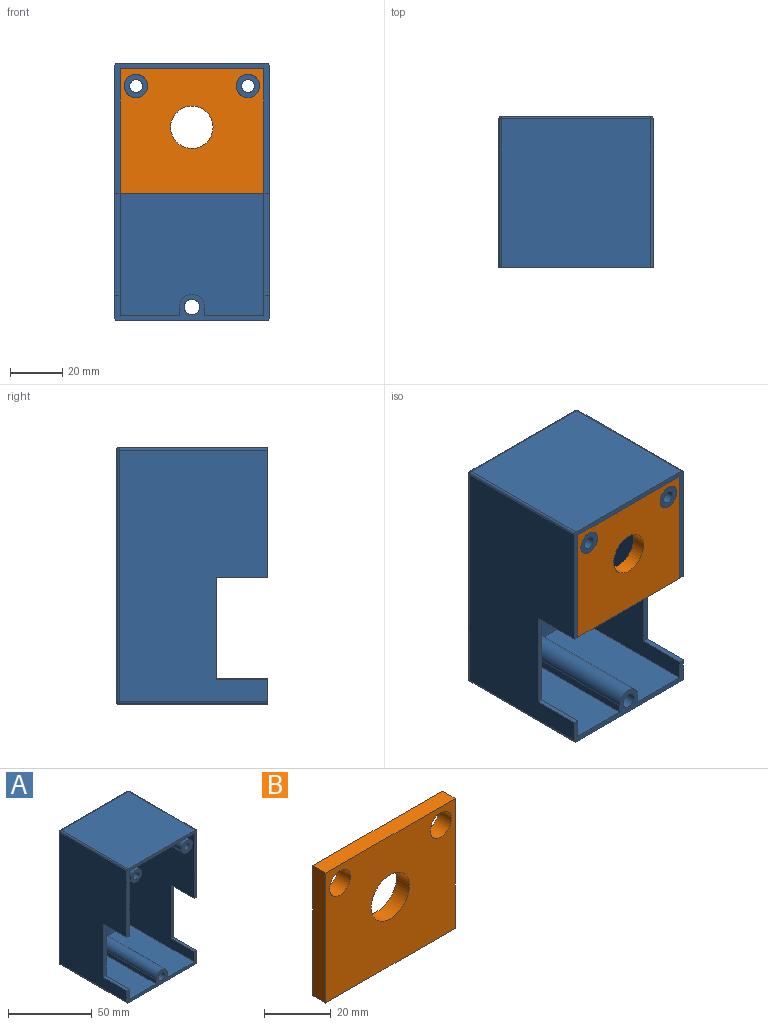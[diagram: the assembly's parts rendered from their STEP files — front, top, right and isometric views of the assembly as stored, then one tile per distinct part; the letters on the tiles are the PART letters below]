
ASSEMBLY  parts=2 mates=1
PART A: 53 faces, bbox 58.9x57.6x98 mm
  f0: cylinder r=15.9mm len=31.11mm, axis (0,1,0), area 179.6mm2, adj f3,f4,f47,f51
  f1: cylinder r=15.9mm len=31.11mm, axis (0,1,0), area 179.6mm2, adj f3,f5,f48,f50
  f2: cylinder r=17.91mm len=35.19mm, axis (0,1,0), area 106.6mm2, adj f4,f7,f47,f51
  f3: plane 96x56.9mm, normal (0,1,0), area 4575.9mm2, adj f0,f1,f15,f17,f34,f38,f39,f43
  f4: plane 35.19x14.59mm, normal (0,-1,0), area 92.9mm2, adj f0,f2,f47,f51
  f5: plane 35.19x14.59mm, normal (0,-1,0), area 92.9mm2, adj f1,f10,f48,f50
  f6: plane 55.55x22.69mm, normal (0,0,1), area 1260.4mm2, adj f7,f18,f19,f31
  f7: plane 94x54.9mm, normal (0,-1,0), area 3963.6mm2, adj f2,f6,f10,f19,f20,f21,f22,f23
  f8: plane 96x56.55mm, normal (1,0,0), area 4668.3mm2, adj f9,f18,f28,f29,f30,f40,f44,f46
  f9: plane 58.9x49.66mm, normal (0,-1,0), area 308mm2, adj f8,f13,f14,f19,f20,f21,f25,f30
  f10: cylinder r=17.91mm len=35.19mm, axis (0,1,0), area 106.6mm2, adj f5,f7,f48,f50
  f11: plane 8.9x8.9mm, normal (0,-1,0), area 43.4mm2, adj f15,f22
  f12: plane 8.9x8.9mm, normal (0,-1,0), area 43.4mm2, adj f17,f24
  f13: plane 56.9x56.55mm, normal (0,0,1), area 3217.7mm2, adj f9,f37,f43,f46
  f14: plane 96x56.55mm, normal (-1,0,0), area 4668.3mm2, adj f9,f18,f25,f26,f27,f35,f37,f38
  f15: cylinder r=2.45mm len=57.55mm, axis (0,1,0), area 885.9mm2, adj f3,f11
  f16: plane 56.9x56.55mm, normal (0,0,-1), area 3217.7mm2, adj f18,f35,f39,f40
  f17: cylinder r=2.45mm len=57.55mm, axis (0,1,0), area 885.9mm2, adj f3,f12
  f18: plane 58.9x9.89mm, normal (0,-1,0), area 184.8mm2, adj f6,f8,f14,f16,f19,f21,f23,f27
  f19: plane 94x55.55mm, normal (-1,0,0), area 4461.2mm2, adj f6,f7,f9,f18,f20,f28,f29,f30
  f20: plane 55.55x54.9mm, normal (0,0,-1), area 3049.7mm2, adj f7,f9,f19,f21
  f21: plane 94x55.55mm, normal (1,0,0), area 4461.2mm2, adj f7,f9,f18,f20,f23,f25,f26,f27
  f22: cylinder r=4.45mm len=55.55mm, axis (0,1,0), area 1553.2mm2, adj f7,f11
  f23: plane 55.55x22.69mm, normal (0,0,1), area 1260.4mm2, adj f7,f18,f21,f33
  f24: cylinder r=4.45mm len=55.55mm, axis (0,1,0), area 1553.2mm2, adj f7,f12
  f25: plane 19.5x2mm, normal (0,0,-1), area 39mm2, adj f9,f14,f21,f26
  f26: plane 39x2mm, normal (0,-1,0), area 78mm2, adj f14,f21,f25,f27
  f27: plane 19.5x2mm, normal (0,0,1), area 39mm2, adj f14,f18,f21,f26
  f28: plane 19.5x2mm, normal (0,0,1), area 39mm2, adj f8,f18,f19,f29
  f29: plane 39x2mm, normal (0,-1,0), area 78mm2, adj f8,f19,f28,f30
  f30: plane 19.5x2mm, normal (0,0,-1), area 39mm2, adj f8,f9,f19,f29
  f31: plane 55.55x3.13mm, normal (1,0,0), area 174mm2, adj f6,f7,f18,f32
  f32: cylinder r=4.76mm len=55.55mm, axis (0,1,0), area 830.7mm2, adj f7,f18,f31,f33
  f33: plane 55.55x3.13mm, normal (-1,0,0), area 174mm2, adj f7,f18,f23,f32
  f34: cylinder r=2.95mm len=57.55mm, axis (0,1,0), area 1066.7mm2, adj f3,f18
  f35: cylinder r=1mm len=56.55mm, axis (0,1,0), area 88.8mm2, adj f14,f16,f18,f36
  f36: sphere r=1mm, area 1.6mm2, adj f35,f38,f39
  f37: cylinder r=1mm len=56.55mm, axis (0,-1,0), area 88.8mm2, adj f9,f13,f14,f41
  f38: cylinder r=1mm len=96mm, axis (0,0,-1), area 150.8mm2, adj f3,f14,f36,f41
  f39: cylinder r=1mm len=56.9mm, axis (1,0,0), area 89.4mm2, adj f3,f16,f36,f42
  f40: cylinder r=1mm len=56.55mm, axis (0,-1,0), area 88.8mm2, adj f8,f16,f18,f42
  f41: sphere r=1mm, area 1.6mm2, adj f37,f38,f43
  f42: sphere r=1mm, area 1.6mm2, adj f39,f40,f44
  f43: cylinder r=1mm len=56.9mm, axis (-1,0,0), area 89.4mm2, adj f3,f13,f41,f45
  f44: cylinder r=1mm len=96mm, axis (0,0,1), area 150.8mm2, adj f3,f8,f42,f45
  f45: sphere r=1mm, area 1.6mm2, adj f43,f44,f46
  f46: cylinder r=1mm len=56.55mm, axis (0,1,0), area 88.8mm2, adj f8,f9,f13,f45
  f47: plane 4.15x2.04mm, normal (0,0,1), area 8.5mm2, adj f0,f2,f3,f4,f49
  f48: plane 4.15x2.04mm, normal (0,0,-1), area 8.5mm2, adj f1,f3,f5,f10,f49
  f49: cylinder r=17.91mm len=6.64mm, axis (0,-1,0), area 13.4mm2, adj f3,f7,f47,f48
  f50: plane 4.15x2.04mm, normal (0,0,-1), area 8.5mm2, adj f1,f3,f5,f10,f52
  f51: plane 4.15x2.04mm, normal (0,0,1), area 8.5mm2, adj f0,f2,f3,f4,f52
  f52: cylinder r=17.91mm len=6.64mm, axis (0,-1,0), area 13.4mm2, adj f3,f7,f50,f51
PART B: 9 faces, bbox 54.9x5.5x47.7 mm
  f0: plane 47.66x5.5mm, normal (-1,0,0), area 262.1mm2, adj f1,f6,f7,f8
  f1: plane 54.9x5.5mm, normal (0,0,-1), area 301.9mm2, adj f0,f2,f7,f8
  f2: plane 47.66x5.5mm, normal (1,0,0), area 262.1mm2, adj f1,f6,f7,f8
  f3: cylinder r=4.45mm len=8.9mm, axis (0,-1,0), area 153.8mm2, adj f7,f8
  f4: cylinder r=4.46mm len=8.92mm, axis (0,-1,0), area 154.2mm2, adj f7,f8
  f5: cylinder r=8.1mm len=16.2mm, axis (0,-1,0), area 279.9mm2, adj f7,f8
  f6: plane 54.9x5.5mm, normal (0,0,1), area 301.9mm2, adj f0,f2,f7,f8
  f7: plane 54.9x47.66mm, normal (0,1,0), area 2285.7mm2, adj f0,f1,f2,f3,f4,f5,f6
  f8: plane 54.9x47.66mm, normal (0,-1,0), area 2285.7mm2, adj f0,f1,f2,f3,f4,f5,f6
PLACE A t=(-50.83,3.02,5.38)mm
PLACE B t=(-50.83,3.02,5.38)mm
MATE fastened B.f2 <-> A.f19  axis (1,0,0) through (-23.38,-54.53,28.55)mm
